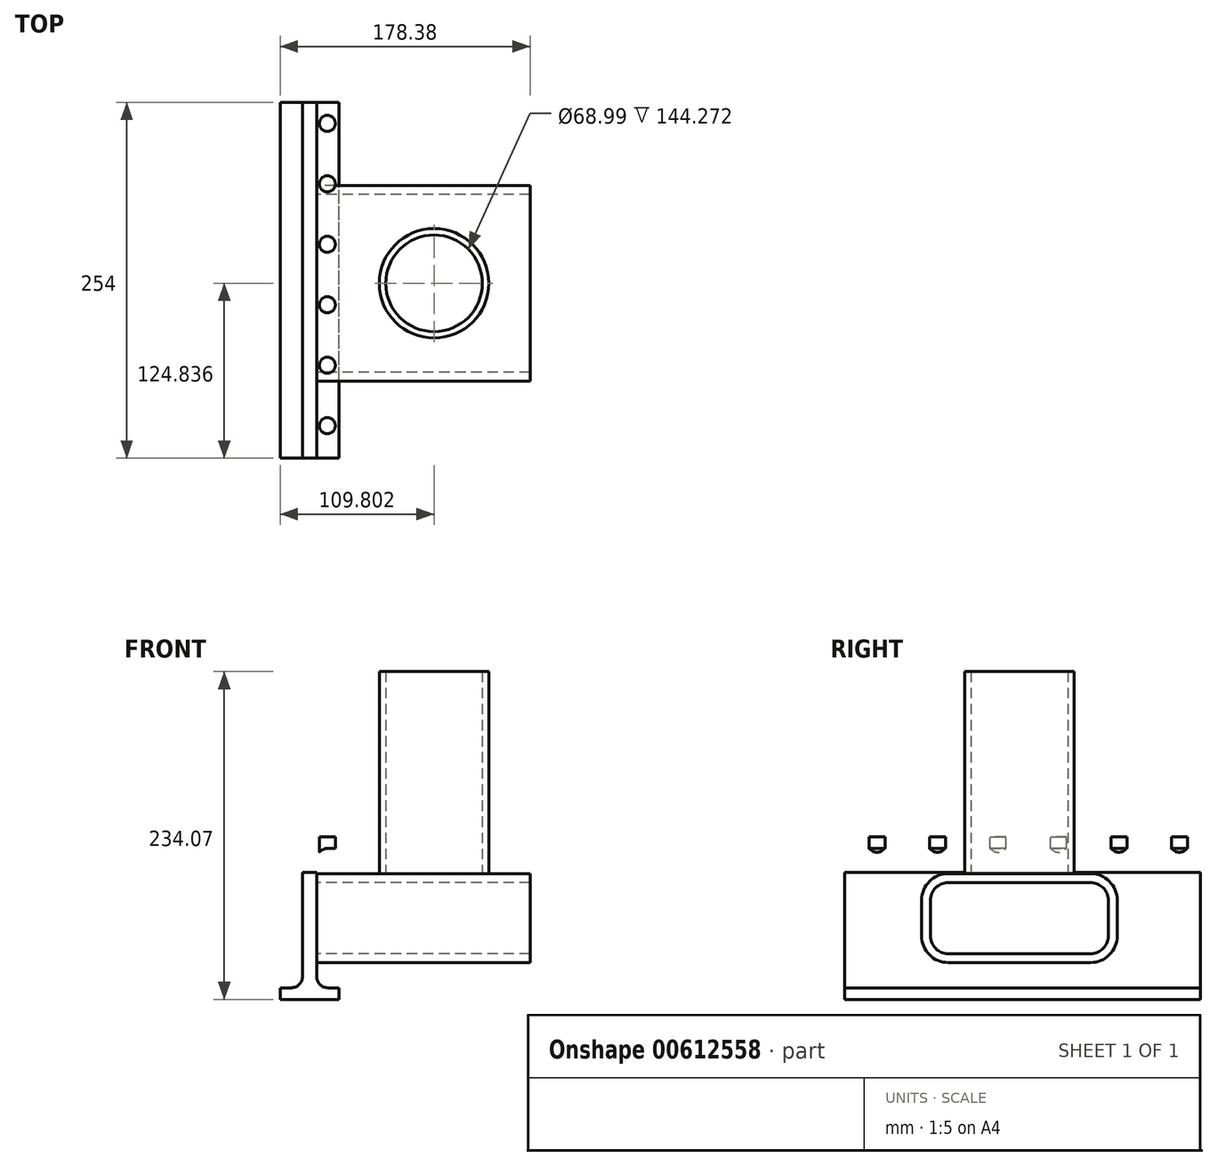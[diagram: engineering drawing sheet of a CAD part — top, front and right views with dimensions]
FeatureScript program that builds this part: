
annotation { "Feature Type Name" : "Feature", "Feature Type Description" : "" }
export const myFeature = defineFeature(function(context is Context, id is Id, definition is map)
    precondition{}
    {
        {
            var Q0;
            Q0=qCreatedBy(makeId("Front.planeOp"),FACE);
            var sketch = newSketch(context, id + "F0", { "sketchPlane" : qUnion([Q0])});
            skLineSegment(sketch, "E0.bottom", {"start": v(5.05, -58.05) * mm, "end": v(-5.05, -58.05) * mm});
            skLineSegment(sketch, "E0.top", {"start": v(5.05, 58.05) * mm, "end": v(-5.05, 58.05) * mm});
            skLineSegment(sketch, "E0.left", {"start": v(5.05, -41.8) * mm, "end": v(5.05, 41.8) * mm});
            skLineSegment(sketch, "E0.right", {"start": v(-5.05, -41.8) * mm, "end": v(-5.05, 41.8) * mm});
            skPoint(sketch, "E0.middle", {"position": v(0, 0) * mm});
            skLineSegment(sketch, "E1.bottom", {"start": v(20.93, -58.05) * mm, "end": v(-20.93, -58.05) * mm});
            skLineSegment(sketch, "E1.top", {"start": v(20.93, -49.8) * mm, "end": v(13.05, -49.8) * mm});
            skLineSegment(sketch, "E1.left", {"start": v(20.93, -58.05) * mm, "end": v(20.93, -49.8) * mm});
            skLineSegment(sketch, "E1.right", {"start": v(-20.93, -58.05) * mm, "end": v(-20.93, -49.8) * mm});
            skPoint(sketch, "E1.middle", {"position": v(0, -53.92) * mm});
            skPoint(sketch, "E1.middle.positionSnap0", {"position": v(0, -58.05) * mm});
            skPoint(sketch, "E1.cornerSnap0", {"position": v(0, -58.05) * mm});
            skPoint(sketch, "E1.centerSnap0", {"position": v(0, -58.05) * mm});
            skLineSegment(sketch, "E2.MirrorCS", {"start": v(20.93, 49.8) * mm, "end": v(13.05, 49.8) * mm});
            skLineSegment(sketch, "E3.MirrorCS", {"start": v(20.93, 58.05) * mm, "end": v(20.93, 49.8) * mm});
            skLineSegment(sketch, "E4.MirrorCS", {"start": v(20.93, 58.05) * mm, "end": v(-20.93, 58.05) * mm});
            skLineSegment(sketch, "E5.MirrorCS", {"start": v(-20.93, 58.05) * mm, "end": v(-20.93, 49.8) * mm});
            skPoint(sketch, "E6.newPointA", {"position": v(-20.93, -49.8) * mm});
            skArc(sketch, "E6.filletArc", {"start": v(5.05, -41.8) * mm, "mid": v(7.4, -47.46) * mm, "end": v(13.05, -49.8) * mm});
            skPoint(sketch, "E7.newPointB", {"position": v(-20.93, 49.8) * mm});
            skArc(sketch, "E7.filletArc", {"start": v(13.05, 49.8) * mm, "mid": v(7.4, 47.46) * mm, "end": v(5.05, 41.8) * mm});
            skLineSegment(sketch, "E8", {"start": v(-20.93, 49.8) * mm, "end": v(-13.05, 49.8) * mm});
            skLineSegment(sketch, "E9", {"start": v(-20.93, -49.8) * mm, "end": v(-13.05, -49.8) * mm});
            skPoint(sketch, "E10.visualSharp", {"position": v(-5.05, 49.8) * mm});
            skArc(sketch, "E10.filletArc", {"start": v(-5.05, 41.8) * mm, "mid": v(-7.4, 47.46) * mm, "end": v(-13.05, 49.8) * mm});
            skPoint(sketch, "E11.visualSharp", {"position": v(-5.05, -49.8) * mm});
            skArc(sketch, "E11.filletArc", {"start": v(-13.05, -49.8) * mm, "mid": v(-7.4, -47.46) * mm, "end": v(-5.05, -41.8) * mm});
            skSolve(sketch);
        }
        {
            var Q0;
            Q0=makeQuery(id+"F0.imprint","IMPRINT",FACE,{"disambiguationData":[TD([[makeQuery(id+"F0.imprint","IMPRINT",EDGE,{"derivedFrom":sQuery(id+"F0.wireOp",EDGE,"E0.left")}),1.0]])]});
            extrude(context, id + "F1", {"entities" : qUnion([Q0]), "depth" : 254 * mm, "offsetDistance" : 25.4 * mm});
        }
        {
            var Q0;
            Q0=makeQuery(id+"F1.opExtrude","SWEPT_FACE",FACE,{"disambiguationData":[OSD([sQuery(id+"F0.wireOp",EDGE,"E4.MirrorCS")])]});
            var sketch = newSketch(context, id + "F2", { "sketchPlane" : qUnion([Q0])});
            skCircle(sketch, "E12", {"center": v(-12.7, -14.96) * mm, "radius": 5.72 * mm});
            skCircle(sketch, "E13.MirrorC", {"center": v(12.7, -14.96) * mm, "radius": 5.72 * mm});
            skCircle(sketch, "E14.1.0.0", {"center": v(-12.7, -58.14) * mm, "radius": 5.72 * mm});
            skCircle(sketch, "E14.2.0.0", {"center": v(-12.7, -101.32) * mm, "radius": 5.72 * mm});
            skCircle(sketch, "E14.3.0.0", {"center": v(-12.7, -144.5) * mm, "radius": 5.72 * mm});
            skCircle(sketch, "E14.4.0.0", {"center": v(-12.7, -187.68) * mm, "radius": 5.72 * mm});
            skCircle(sketch, "E14.5.0.0", {"center": v(-12.7, -230.86) * mm, "radius": 5.72 * mm});
            skLineSegment(sketch, "E14.direction1", {"start": v(-12.7, -14.96) * mm, "end": v(-12.7, -58.14) * mm, "construction": true});
            skCircle(sketch, "E15.MirrorC", {"center": v(12.7, -58.14) * mm, "radius": 5.72 * mm});
            skCircle(sketch, "E16.MirrorC", {"center": v(12.7, -101.32) * mm, "radius": 5.72 * mm});
            skCircle(sketch, "E17.MirrorC", {"center": v(12.7, -144.5) * mm, "radius": 5.72 * mm});
            skCircle(sketch, "E18.MirrorC", {"center": v(12.7, -187.68) * mm, "radius": 5.72 * mm});
            skCircle(sketch, "E19.MirrorC", {"center": v(12.7, -230.86) * mm, "radius": 5.72 * mm});
            skSolve(sketch);
        }
        {
            var Q0;
            Q0=makeQuery(id+"F2.imprint","IMPRINT",FACE,{"disambiguationData":[TD([[makeQuery(id+"F2.imprint","IMPRINT",EDGE,{"derivedFrom":sQuery(id+"F2.wireOp",EDGE,"E13.MirrorC")}),-1.0]])]});
            var Q1;
            Q1=makeQuery(id+"F2.imprint","IMPRINT",FACE,{"disambiguationData":[TD([[makeQuery(id+"F2.imprint","IMPRINT",EDGE,{"derivedFrom":sQuery(id+"F2.wireOp",EDGE,"E15.MirrorC")}),-1.0]])]});
            var Q2;
            Q2=makeQuery(id+"F2.imprint","IMPRINT",FACE,{"disambiguationData":[TD([[makeQuery(id+"F2.imprint","IMPRINT",EDGE,{"derivedFrom":sQuery(id+"F2.wireOp",EDGE,"E16.MirrorC")}),-1.0]])]});
            var Q3;
            Q3=makeQuery(id+"F2.imprint","IMPRINT",FACE,{"disambiguationData":[TD([[makeQuery(id+"F2.imprint","IMPRINT",EDGE,{"derivedFrom":sQuery(id+"F2.wireOp",EDGE,"E17.MirrorC")}),-1.0]])]});
            var Q4;
            Q4=makeQuery(id+"F2.imprint","IMPRINT",FACE,{"disambiguationData":[TD([[makeQuery(id+"F2.imprint","IMPRINT",EDGE,{"derivedFrom":sQuery(id+"F2.wireOp",EDGE,"E18.MirrorC")}),-1.0]])]});
            var Q5;
            Q5=makeQuery(id+"F2.imprint","IMPRINT",FACE,{"disambiguationData":[TD([[makeQuery(id+"F2.imprint","IMPRINT",EDGE,{"derivedFrom":sQuery(id+"F2.wireOp",EDGE,"E19.MirrorC")}),-1.0]])]});
            var Q6;
            Q6=makeQuery(id+"F2.imprint","IMPRINT",FACE,{"disambiguationData":[TD([[makeQuery(id+"F2.imprint","IMPRINT",EDGE,{"derivedFrom":sQuery(id+"F2.wireOp",EDGE,"E14.5.0.0")}),1.0]])]});
            var Q7;
            Q7=makeQuery(id+"F2.imprint","IMPRINT",FACE,{"disambiguationData":[TD([[makeQuery(id+"F2.imprint","IMPRINT",EDGE,{"derivedFrom":sQuery(id+"F2.wireOp",EDGE,"E14.4.0.0")}),1.0]])]});
            var Q8;
            Q8=makeQuery(id+"F2.imprint","IMPRINT",FACE,{"disambiguationData":[TD([[makeQuery(id+"F2.imprint","IMPRINT",EDGE,{"derivedFrom":sQuery(id+"F2.wireOp",EDGE,"E14.3.0.0")}),1.0]])]});
            var Q9;
            Q9=makeQuery(id+"F2.imprint","IMPRINT",FACE,{"disambiguationData":[TD([[makeQuery(id+"F2.imprint","IMPRINT",EDGE,{"derivedFrom":sQuery(id+"F2.wireOp",EDGE,"E14.2.0.0")}),1.0]])]});
            var Q10;
            Q10=makeQuery(id+"F2.imprint","IMPRINT",FACE,{"disambiguationData":[TD([[makeQuery(id+"F2.imprint","IMPRINT",EDGE,{"derivedFrom":sQuery(id+"F2.wireOp",EDGE,"E14.1.0.0")}),1.0]])]});
            var Q11;
            Q11=makeQuery(id+"F2.imprint","IMPRINT",FACE,{"disambiguationData":[TD([[makeQuery(id+"F2.imprint","IMPRINT",EDGE,{"derivedFrom":sQuery(id+"F2.wireOp",EDGE,"E12")}),1.0]])]});
            extrude(context, id + "F3", {"entities" : qUnion([Q0, Q1, Q2, Q3, Q4, Q5, Q6, Q7, Q8, Q9, Q10, Q11]), "operationType" : NewBodyOperationType.REMOVE, "oppositeDirection" : true, "depth" : 25.4 * mm, "offsetDistance" : 25.4 * mm});
        }
        {
            var Q0;
            Q0=makeQuery(id+"F1.opExtrude","SWEPT_FACE",FACE,{"disambiguationData":[OSD([sQuery(id+"F0.wireOp",EDGE,"E0.left")])]});
            var sketch = newSketch(context, id + "F4", { "sketchPlane" : qUnion([Q0])});
            skLineSegment(sketch, "E20.bottom", {"start": v(-78.36, -25.4) * mm, "end": v(-179.96, -25.4) * mm});
            skLineSegment(sketch, "E20.top", {"start": v(-78.36, 25.4) * mm, "end": v(-179.96, 25.4) * mm});
            skLineSegment(sketch, "E20.left", {"start": v(-65.66, -12.7) * mm, "end": v(-65.66, 12.7) * mm});
            skLineSegment(sketch, "E20.right", {"start": v(-192.66, -12.7) * mm, "end": v(-192.66, 12.7) * mm});
            skPoint(sketch, "E20.middle", {"position": v(-129.16, 0) * mm});
            skPoint(sketch, "E21.visualSharp", {"position": v(-192.66, 25.4) * mm});
            skArc(sketch, "E21.filletArc", {"start": v(-179.96, 25.4) * mm, "mid": v(-188.94, 21.68) * mm, "end": v(-192.66, 12.7) * mm});
            skPoint(sketch, "E22.visualSharp", {"position": v(-192.66, -25.4) * mm});
            skArc(sketch, "E22.filletArc", {"start": v(-192.66, -12.7) * mm, "mid": v(-188.94, -21.68) * mm, "end": v(-179.96, -25.4) * mm});
            skPoint(sketch, "E23.visualSharp", {"position": v(-65.66, -25.4) * mm});
            skArc(sketch, "E23.filletArc", {"start": v(-78.36, -25.4) * mm, "mid": v(-69.38, -21.68) * mm, "end": v(-65.66, -12.7) * mm});
            skPoint(sketch, "E24.visualSharp", {"position": v(-65.66, 25.4) * mm});
            skArc(sketch, "E24.filletArc", {"start": v(-65.66, 12.7) * mm, "mid": v(-69.38, 21.68) * mm, "end": v(-78.36, 25.4) * mm});
            skArc(sketch, "E25.0", {"start": v(-59.31, 12.7) * mm, "mid": v(-64.9, 26.17) * mm, "end": v(-78.36, 31.75) * mm});
            skLineSegment(sketch, "E25.1", {"start": v(-59.31, -12.7) * mm, "end": v(-59.31, 12.7) * mm});
            skLineSegment(sketch, "E25.2", {"start": v(-78.36, 31.75) * mm, "end": v(-179.96, 31.75) * mm});
            skArc(sketch, "E25.3", {"start": v(-78.36, -31.75) * mm, "mid": v(-64.9, -26.17) * mm, "end": v(-59.31, -12.7) * mm});
            skArc(sketch, "E25.4", {"start": v(-179.96, 31.75) * mm, "mid": v(-193.43, 26.17) * mm, "end": v(-199.01, 12.7) * mm});
            skLineSegment(sketch, "E25.5", {"start": v(-199.01, -12.7) * mm, "end": v(-199.01, 12.7) * mm});
            skArc(sketch, "E25.6", {"start": v(-199.01, -12.7) * mm, "mid": v(-193.43, -26.17) * mm, "end": v(-179.96, -31.75) * mm});
            skLineSegment(sketch, "E25.7", {"start": v(-78.36, -31.75) * mm, "end": v(-179.96, -31.75) * mm});
            skSolve(sketch);
        }
        {
            var Q0;
            Q0=makeQuery(id+"F4.imprint","IMPRINT",FACE,{"disambiguationData":[TD([[makeQuery(id+"F4.imprint","IMPRINT",EDGE,{"derivedFrom":sQuery(id+"F4.wireOp",EDGE,"E20.bottom")}),1.0]])]});
            extrude(context, id + "F5", {"entities" : qUnion([Q0]), "operationType" : NewBodyOperationType.ADD, "depth" : 152.4 * mm, "offsetDistance" : 25.4 * mm});
        }
        {
            var Q0;
            Q0=makeQuery(id+"F5.opExtrude","SWEPT_FACE",FACE,{"disambiguationData":[OSD([sQuery(id+"F4.wireOp",EDGE,"E25.2")])]});
            var sketch = newSketch(context, id + "F6", { "sketchPlane" : qUnion([Q0])});
            skPoint(sketch, "E26.endSnap0", {"position": v(157.45, -129.16) * mm});
            skCircle(sketch, "E27", {"center": v(88.87, -129.16) * mm, "radius": 39.08 * mm});
            skCircle(sketch, "E28", {"center": v(88.87, -129.16) * mm, "radius": 34.5 * mm});
            skSolve(sketch);
        }
        {
            var Q0;
            Q0=makeQuery(id+"F6.imprint","IMPRINT",FACE,{"disambiguationData":[TD([[makeQuery(id+"F6.imprint","IMPRINT",EDGE,{"derivedFrom":sQuery(id+"F6.wireOp",EDGE,"E27")}),1.0]])]});
            extrude(context, id + "F7", {"entities" : qUnion([Q0]), "operationType" : NewBodyOperationType.ADD, "depth" : 144.27 * mm, "offsetDistance" : 25.4 * mm});
        }
    });
